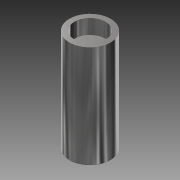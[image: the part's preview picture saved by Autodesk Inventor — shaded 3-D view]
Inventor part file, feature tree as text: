
AUTODESK INVENTOR PART (.ipt)
format: ipt  version: 2014 SP2 (Build 180246200, 246)  size: 119,296 bytes
history: native  units: mm
features: extrude x5, sketch x5, plane x1, thread x1, fillet x1, projected_geometry x1
ambient origin geometry x8: Origin, YZ Plane, XZ Plane, XY Plane, X Axis, Y Axis, Z Axis, Center Point
bodies: Solid1 (feature_tree)
feature tree (14):
  extrude  "Extrusion1"  Depth=35.0mm TaperAngle=0.0deg
  extrude  "Extrusion2"  Depth=9.0mm TaperAngle=0.0deg
  extrude  "Extrusion3"  Depth=9.0mm TaperAngle=0.0deg
  extrude  "Extrusion4"  Depth=0.4mm
  plane  "Work Plane1"
  extrude  "Extrusion5"  [1 undecoded]
  thread  "Thread1"  [1 undecoded]
  fillet  "Fillet1"  [1 undecoded]
  sketch  "Sketch1"  dims[d1=35.0mm d2=0.0mm d4=5.0mm d5=0.0mm]
  sketch  "Sketch2"  dims[d7=30.0mm d8=0.0mm d10=9.0mm d11=0.0mm]
  sketch  "Sketch3"  dims[d12=9.0mm d15=9.0mm d16=0.0mm]
  sketch  "Sketch4"  dims[d17=10.0mm d18=0.0mm d19=0.4mm]
  sketch  "Sketch5"
  projected_geometry  "Projected Loop1"
note: 3 required parameter values undecoded (feature->parameter linkage not recoverable at this tier; creation-order binding heuristic only, values carry confidence <= 0.55)
